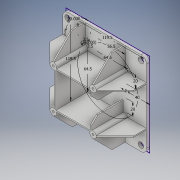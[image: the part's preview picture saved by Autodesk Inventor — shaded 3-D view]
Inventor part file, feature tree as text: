
AUTODESK INVENTOR PART (.ipt)
format: ipt  version: 2019.3 (Build 233278000, 278)  size: 248,832 bytes
history: native  units: mm
features: extrude x2, chamfer x2, other x1, fillet x1
ambient origin geometry x8: Origin, YZ Plane, XZ Plane, XY Plane, X Axis, Y Axis, Z Axis, Center Point
bodies: Body1 (feature_tree)
feature tree (6):
  other  "BasePlate"
  extrude  "Extrusion8"  Depth=56.5mm
  extrude  "Extrusion9"  Depth=40.0mm
  chamfer  "Chamfer3"  Distance=3.5mm
  chamfer  "Chamfer4"  Distance=3.5mm
  fillet  "Fillet3"  Radius=4.0mm
